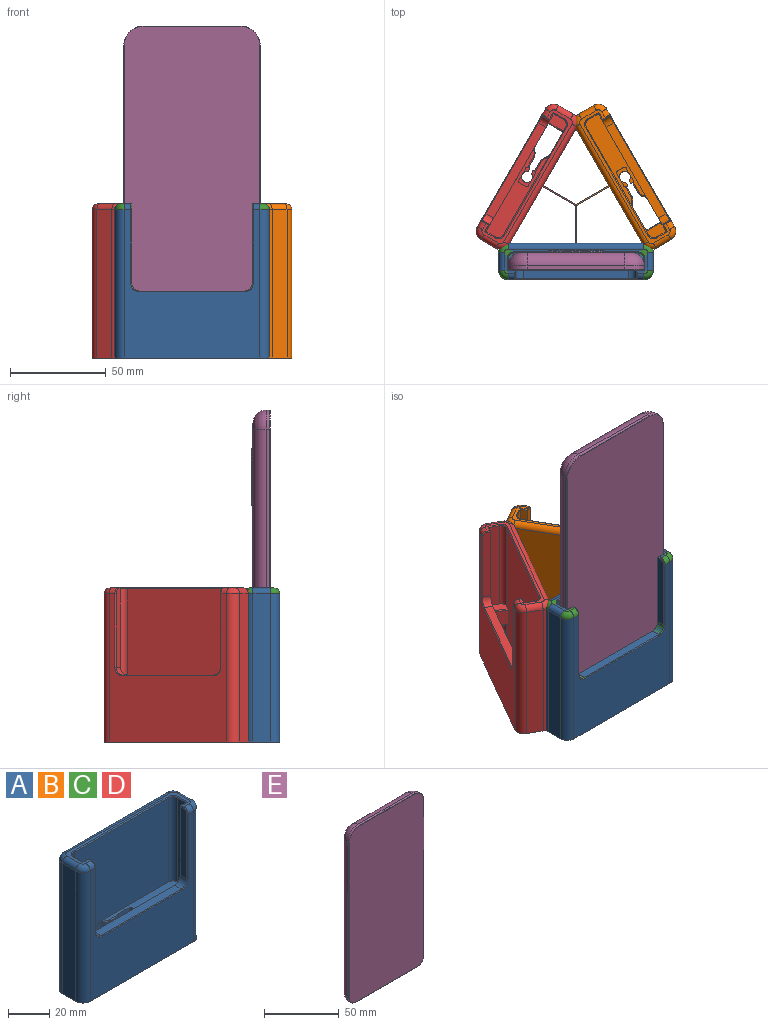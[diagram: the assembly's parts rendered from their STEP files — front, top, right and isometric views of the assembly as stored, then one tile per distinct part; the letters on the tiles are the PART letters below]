
ASSEMBLY  parts=5 mates=1
PART A: 91 faces, bbox 81.1x39.3x80.9 mm
  f0: plane 20x5.98mm, normal (1,0,0), area 119.6mm2, adj f2,f3,f14,f82
  f1: plane 80.12x65.06mm, normal (0,-1,0), area 4437.7mm2, adj f3,f14,f24,f25,f29,f30,f31,f37
  f2: plane 80.12x71.06mm, normal (0,1,0), area 2017.3mm2, adj f0,f5,f6,f7,f12,f13,f14,f24
  f3: cylinder r=3mm len=20mm, axis (0,0,1), area 94.2mm2, adj f0,f1,f14,f82
  f4: plane 74.94x12.98mm, normal (0,0,1), area 160.7mm2, adj f32,f33,f34,f35,f36,f37,f38,f39
  f5: plane 15x5.98mm, normal (-1,0,0), area 89.7mm2, adj f2,f14,f25,f29
  f6: plane 50x5.98mm, normal (-1,0,0), area 299mm2, adj f2,f24,f30,f40
  f7: plane 41x4.5mm, normal (-1,0,0), area 183.2mm2, adj f2,f28,f44,f46,f48
  f8: plane 77.5x8.98mm, normal (1,0,0), area 696mm2, adj f14,f33,f53,f59
  f9: plane 77.5x70.94mm, normal (0,1,0), area 5497.6mm2, adj f14,f34,f57,f59,f86,f88,f89,f90
  f10: plane 77.5x8.98mm, normal (-1,0,0), area 696mm2, adj f14,f35,f55,f57
  f11: plane 77.5x70.94mm, normal (0,-1,0), area 2757.1mm2, adj f14,f32,f36,f48,f49,f50,f51,f52
  f12: plane 41x4.5mm, normal (1,0,0), area 183.2mm2, adj f2,f27,f45,f47,f49
  f13: plane 50x5.98mm, normal (1,0,0), area 299mm2, adj f2,f31,f41,f81
  f14: plane 80.94x18.98mm, normal (0,0,-1), area 881.6mm2, adj f0,f1,f2,f3,f5,f8,f9,f10
  f15: plane 10x7.37mm, normal (0,1,0), area 73.7mm2, adj f16,f23,f24,f62,f66
  f16: cylinder r=1mm len=10mm, axis (0,0,-1), area 15.7mm2, adj f15,f17,f24,f66,f78
  f17: plane 14.5x5.61mm, normal (0,1,0), area 81.4mm2, adj f16,f25,f65,f71,f78
  f18: plane 14.5x5.61mm, normal (0,-1,0), area 81.4mm2, adj f19,f25,f67,f72,f75
  f19: cylinder r=1mm len=10mm, axis (0,0,-1), area 15.7mm2, adj f18,f20,f24,f70,f75
  f20: plane 10x7.37mm, normal (0,-1,0), area 73.7mm2, adj f19,f21,f24,f62,f70
  f21: cylinder r=1mm len=10mm, axis (0,0,-1), area 15.7mm2, adj f20,f22,f24,f62
  f22: plane 10x3.78mm, normal (-1,0,0), area 37.8mm2, adj f21,f23,f24,f62
  f23: cylinder r=1mm len=10mm, axis (0,0,-1), area 15.7mm2, adj f15,f22,f24,f62
  f24: plane 49.87x8.98mm, normal (0,0,1), area 340.4mm2, adj f1,f2,f6,f15,f16,f19,f20,f21
  f25: plane 51.67x8.98mm, normal (0,0,-1), area 374.7mm2, adj f1,f2,f5,f17,f18,f29,f61,f63
  f26: plane 54.94x4.5mm, normal (0,0,1), area 247.2mm2, adj f2,f27,f28,f52
  f27: cylinder r=4mm len=4.5mm, axis (0,1,0), area 28.3mm2, adj f2,f12,f26,f51
  f28: cylinder r=4mm len=4.5mm, axis (0,-1,0), area 28.3mm2, adj f2,f7,f26,f50
  f29: cylinder r=3mm len=15mm, axis (0,0,-1), area 70.7mm2, adj f1,f5,f14,f25
  f30: cylinder r=3mm len=50mm, axis (0,0,-1), area 235.6mm2, adj f1,f6,f24,f38
  f31: cylinder r=3mm len=50mm, axis (0,0,1), area 235.6mm2, adj f1,f13,f39,f81
  f32: cylinder r=3mm len=3.5mm, axis (-1,0,0), area 16.5mm2, adj f4,f11,f46,f54
  f33: cylinder r=3mm len=8.98mm, axis (0,-1,0), area 42.3mm2, adj f4,f8,f54,f60
  f34: cylinder r=3mm len=70.94mm, axis (1,0,0), area 334.3mm2, adj f4,f9,f58,f60
  f35: cylinder r=3mm len=8.98mm, axis (0,1,0), area 42.3mm2, adj f4,f10,f56,f58
  f36: cylinder r=3mm len=3.5mm, axis (-1,0,0), area 16.5mm2, adj f4,f11,f47,f56
  f37: cylinder r=0.5mm len=64.94mm, axis (-1,0,0), area 51mm2, adj f1,f4,f38,f39
  f38: torus R=3.5mm, axis (0,0,1), area 3.9mm2, adj f4,f30,f37,f40
  f39: torus R=3.5mm, axis (0,0,1), area 3.9mm2, adj f4,f31,f37,f41
  f40: cylinder r=0.5mm len=6.48mm, axis (0,1,0), area 4.9mm2, adj f4,f6,f38,f42
  f41: cylinder r=0.5mm len=6.48mm, axis (0,-1,0), area 4.9mm2, adj f4,f13,f39,f43
  f42: cylinder r=0.5mm len=4.5mm, axis (1,0,0), area 3.1mm2, adj f2,f4,f40,f44
  f43: cylinder r=0.5mm len=4.5mm, axis (1,0,0), area 3.1mm2, adj f2,f4,f41,f45
  f44: cylinder r=0.5mm len=2mm, axis (0,1,0), area 1.4mm2, adj f4,f7,f42,f46
  f45: cylinder r=0.5mm len=2mm, axis (0,-1,0), area 1.4mm2, adj f4,f12,f43,f47
  f46: torus R=2.5mm, axis (1,0,0), area 3.5mm2, adj f7,f32,f44,f48
  f47: torus R=2.5mm, axis (1,0,0), area 3.5mm2, adj f12,f36,f45,f49
  f48: cylinder r=0.5mm len=38.5mm, axis (0,0,1), area 30.2mm2, adj f7,f11,f46,f50
  f49: cylinder r=0.5mm len=38.5mm, axis (0,0,-1), area 30.2mm2, adj f11,f12,f47,f51
  f50: torus R=4.5mm, axis (0,-1,0), area 5.2mm2, adj f11,f28,f48,f52
  f51: torus R=4.5mm, axis (0,-1,0), area 5.2mm2, adj f11,f27,f49,f52
  f52: cylinder r=0.5mm len=54.94mm, axis (-1,0,0), area 43.1mm2, adj f11,f26,f50,f51
  f53: cylinder r=5mm len=77.5mm, axis (0,0,-1), area 608.7mm2, adj f8,f11,f14,f54
  f54: torus R=2mm, axis (0,0,1), area 28.9mm2, adj f4,f32,f33,f53
  f55: cylinder r=5mm len=77.5mm, axis (0,0,1), area 608.7mm2, adj f10,f11,f14,f56
  f56: torus R=2mm, axis (0,0,1), area 28.9mm2, adj f4,f35,f36,f55
  f57: cylinder r=5mm len=77.5mm, axis (0,0,-1), area 608.7mm2, adj f9,f10,f14,f58
  f58: torus R=2mm, axis (0,0,1), area 28.9mm2, adj f4,f34,f35,f57
  f59: cylinder r=5mm len=77.5mm, axis (0,0,1), area 608.7mm2, adj f8,f9,f14,f60
  f60: torus R=2mm, axis (0,0,1), area 28.9mm2, adj f4,f33,f34,f59
  f61: cylinder r=2.89mm len=5.78mm, axis (0,0,1), area 80.5mm2, adj f25,f62,f63,f66,f69,f70
  f62: plane 5.78x4.68mm, normal (0,0,1), area 13.5mm2, adj f15,f20,f21,f22,f23,f61
  f63: plane 5x1.47mm, normal (0,1,0), area 7.4mm2, adj f25,f61,f64,f66
  f64: cylinder r=0.5mm len=5mm, axis (0,0,1), area 3.9mm2, adj f25,f63,f65,f66
  f65: plane 5x0.39mm, normal (-1,0,0), area 1.9mm2, adj f17,f25,f64,f66
  f66: plane 4.68x1.89mm, normal (0,0,1), area 4.9mm2, adj f15,f16,f61,f63,f64,f65
  f67: plane 5x0.39mm, normal (-1,0,0), area 1.9mm2, adj f18,f25,f68,f70
  f68: cylinder r=0.5mm len=5mm, axis (0,0,1), area 3.9mm2, adj f25,f67,f69,f70
  f69: plane 5x1.47mm, normal (0,-1,0), area 7.4mm2, adj f25,f61,f68,f70
  f70: plane 4.68x1.89mm, normal (0,0,1), area 4.9mm2, adj f19,f20,f61,f67,f68,f69
  f71: cylinder r=5mm len=14.5mm, axis (0,0,-1), area 60.2mm2, adj f17,f25,f73,f79
  f72: cylinder r=5mm len=14.5mm, axis (0,0,-1), area 60.2mm2, adj f18,f25,f74,f76
  f73: cylinder r=3mm len=14.5mm, axis (0,0,-1), area 36.1mm2, adj f2,f25,f71,f80
  f74: cylinder r=3mm len=14.5mm, axis (0,0,-1), area 36.1mm2, adj f1,f25,f72,f77
  f75: cylinder r=0.5mm len=5.75mm, axis (-1,0,0), area 4.5mm2, adj f18,f19,f24,f76
  f76: torus R=4.5mm, axis (0,0,1), area 3.1mm2, adj f24,f72,f75,f77
  f77: torus R=3.5mm, axis (0,0,1), area 1.4mm2, adj f1,f24,f74,f76
  f78: cylinder r=0.5mm len=5.75mm, axis (1,0,0), area 4.5mm2, adj f16,f17,f24,f79
  f79: torus R=4.5mm, axis (0,0,1), area 3.1mm2, adj f24,f71,f78,f80
  f80: torus R=3.5mm, axis (0,0,1), area 1.4mm2, adj f2,f24,f73,f79
  f81: plane 8.98x5.29mm, normal (0,0,1), area 45.6mm2, adj f1,f2,f13,f31,f85
  f82: plane 8.98x5.29mm, normal (0,0,-1), area 45.6mm2, adj f0,f1,f2,f3,f84
  f83: plane 9x8.98mm, normal (1,0,0), area 80.8mm2, adj f1,f2,f84,f85
  f84: cylinder r=0.5mm len=8.98mm, axis (0,1,0), area 7.1mm2, adj f1,f2,f82,f83
  f85: cylinder r=0.5mm len=8.98mm, axis (0,-1,0), area 7.1mm2, adj f1,f2,f81,f83
  f86: plane 20x0.5mm, normal (1,0,0), area 10mm2, adj f9,f87,f89,f90
  f87: plane 0.5x0.5mm, normal (0,1,0), area 0.2mm2, adj f86,f88,f89,f90
  f88: plane 20x0.5mm, normal (-1,0,0), area 10mm2, adj f9,f87,f89,f90
  f89: plane 20x0.5mm, normal (0,0,1), area 10mm2, adj f9,f86,f87,f88
  f90: plane 20x0.5mm, normal (0,0,-1), area 10mm2, adj f9,f86,f87,f88
PART B: same geometry as A
PART C: same geometry as A
PART D: same geometry as A
PART E: 43 faces, bbox 72.8x10x144.9 mm
  f0: cylinder r=7mm len=57.18mm, axis (-1,0,0), area 610.4mm2, adj f2,f6,f22,f25,f30,f31,f32,f33
  f1: plane 126.5x1.76mm, normal (1,0,0), area 222.6mm2, adj f8,f10,f13,f20
  f2: plane 129.5x57.18mm, normal (0,1,0), area 6694.1mm2, adj f0,f19,f20,f21,f23,f24,f26
  f3: plane 126.5x1.76mm, normal (-1,0,0), area 222.6mm2, adj f7,f9,f16,f24
  f4: plane 143.1x70.78mm, normal (0,-1,0), area 10067.6mm2, adj f11,f12,f13,f14,f15,f16,f17,f18
  f5: plane 51.18x1.76mm, normal (0,0,1), area 90.1mm2, adj f7,f8,f12,f21
  f6: plane 57.18x1.76mm, normal (0,0,-1), area 100.6mm2, adj f0,f9,f10,f17
  f7: cylinder r=10mm len=10mm, axis (0,1,0), area 27.6mm2, adj f3,f5,f14,f23
  f8: cylinder r=10mm len=10mm, axis (0,-1,0), area 27.6mm2, adj f1,f5,f11,f19
  f9: cylinder r=7mm len=7mm, axis (0,-1,0), area 19.4mm2, adj f3,f6,f18,f25
  f10: cylinder r=7mm len=7mm, axis (0,1,0), area 19.4mm2, adj f1,f6,f15,f22
  f11: torus R=9.8mm, axis (0,-1,0), area 4.9mm2, adj f4,f8,f12,f13
  f12: cylinder r=0.2mm len=51.18mm, axis (-1,0,0), area 16.1mm2, adj f4,f5,f11,f14
  f13: cylinder r=0.2mm len=126.5mm, axis (0,0,-1), area 39.7mm2, adj f1,f4,f11,f15
  f14: torus R=9.8mm, axis (0,-1,0), area 4.9mm2, adj f4,f7,f12,f16
  f15: torus R=6.8mm, axis (0,-1,0), area 3.4mm2, adj f4,f10,f13,f17
  f16: cylinder r=0.2mm len=126.5mm, axis (0,0,1), area 39.7mm2, adj f3,f4,f14,f18
  f17: cylinder r=0.2mm len=57.18mm, axis (1,0,0), area 18mm2, adj f4,f6,f15,f18
  f18: torus R=6.8mm, axis (0,-1,0), area 3.4mm2, adj f4,f9,f16,f17
  f19: torus R=3mm, axis (0,-1,0), area 128.8mm2, adj f2,f8,f20,f21
  f20: cylinder r=7mm len=126.5mm, axis (0,0,1), area 1390.9mm2, adj f1,f2,f19,f22
  f21: cylinder r=7mm len=51.18mm, axis (1,0,0), area 562.8mm2, adj f2,f5,f19,f23
  f22: sphere r=7mm, area 77mm2, adj f0,f10,f20
  f23: torus R=3mm, axis (0,-1,0), area 128.8mm2, adj f2,f7,f21,f24
  f24: cylinder r=7mm len=126.5mm, axis (0,0,-1), area 1390.9mm2, adj f2,f3,f23,f25
  f25: sphere r=7mm, area 77mm2, adj f0,f9,f24
  f26: cylinder r=15mm len=30mm, axis (0,-1,0), area 27.6mm2, adj f2,f29
  f27: plane 29x29mm, normal (0,1,0), area 660.5mm2, adj f28
  f28: cone r=14.5mm half-angle=45deg, axis (0,-1,0), area 46.1mm2, adj f27,f29
  f29: torus R=14.5mm, axis (0,1,0), area 36.9mm2, adj f26,f28
  f30: cylinder r=0.3mm len=3.95mm, axis (0,0,-1), area 0.9mm2, adj f0,f31,f41,f42
  f31: plane 4.61x3.9mm, normal (0,-1,0), area 18mm2, adj f0,f30,f32,f42
  f32: cylinder r=0.3mm len=3.95mm, axis (0,0,-1), area 0.9mm2, adj f0,f31,f33,f42
  f33: plane 4.5x1.14mm, normal (0.69,-0.73,0), area 6.7mm2, adj f0,f32,f34,f42
  f34: cylinder r=0.3mm len=4.58mm, axis (0,0,-1), area 1.1mm2, adj f0,f33,f35,f42
  f35: plane 4.8x0.73mm, normal (1,0,0), area 3.4mm2, adj f0,f34,f36,f42
  f36: cylinder r=0.39mm len=4.88mm, axis (0,0,-1), area 3mm2, adj f0,f35,f37,f42
  f37: plane 6.71x4.88mm, normal (0,1,0), area 32.8mm2, adj f0,f36,f38,f42
  f38: cylinder r=0.39mm len=4.88mm, axis (0,0,-1), area 3mm2, adj f0,f37,f39,f42
  f39: plane 4.8x0.73mm, normal (-1,0,0), area 3.4mm2, adj f0,f38,f40,f42
  f40: cylinder r=0.3mm len=4.58mm, axis (0,0,-1), area 1.1mm2, adj f0,f39,f41,f42
  f41: plane 4.5x1.14mm, normal (-0.69,-0.73,0), area 6.7mm2, adj f0,f30,f40,f42
  f42: plane 7.5x2.5mm, normal (0,0,-1), area 17mm2, adj f30,f31,f32,f33,f34,f35,f36,f37
PLACE A t=(-12.55,11.3,31.48)mm
PLACE B rot(axis=(0,0,1),120deg) t=(12.99,55.54,31.48)mm
PLACE C t=(-12.55,11.3,31.48)mm
PLACE D rot(axis=(0,0,-1),120deg) t=(-38.09,55.54,31.48)mm
PLACE E t=(-12.55,11.3,41.48)mm
MATE fastened E.f6 <-> C.f61  axis (0,0,-1) through (-12.55,11.3,41.48)mm
